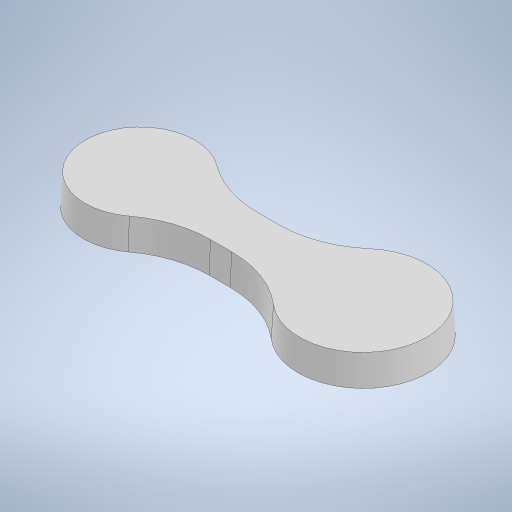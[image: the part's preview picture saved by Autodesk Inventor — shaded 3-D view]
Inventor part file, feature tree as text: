
AUTODESK INVENTOR PART (.ipt)
format: ipt  version: 2023 (Build 270158000, 158)  size: 272,896 bytes
history: native  units: in
note: dims shown in document units (in); Inventor stores cm internally (conversion verified against a paired STEP export)
features: extrude x1, fillet x1, draft x1, sketch x1
ambient origin geometry x8: Origin, YZ Plane, XZ Plane, XY Plane, X Axis, Y Axis, Z Axis, Center Point
bodies: Body1 (feature_tree)
feature tree (4):
  extrude  "Extrusion2"  Depth=1.0in
  fillet  "Fillet3"  Radius=1.3in
  draft  "FaceDraft2"
  sketch  "Sketch1"  dims[d15=0.872in d17=0.5in d18=1.3in d19=0.76in d20=1.125in d21=2.225in d22=0.3in d23=0.0in d27=1.0in d28=0.0206in d3=0.5in d4=0.0344in d5=0.5in d6=0.0344in d29=0.0in d30=0.0in d31=0.0in]
